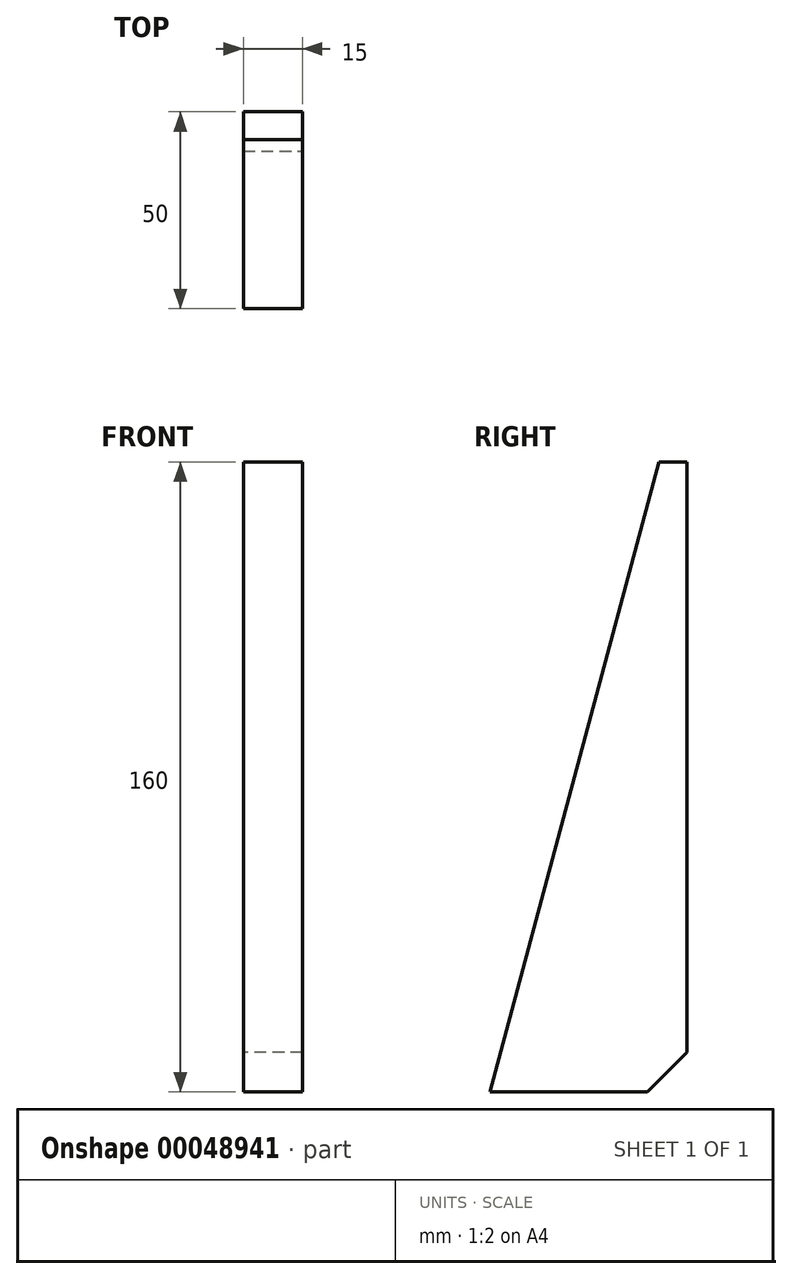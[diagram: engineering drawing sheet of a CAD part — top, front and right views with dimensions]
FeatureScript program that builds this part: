
annotation { "Feature Type Name" : "Feature", "Feature Type Description" : "" }
export const myFeature = defineFeature(function(context is Context, id is Id, definition is map)
    precondition{}
    {
        {
            var Q0;
            Q0=qCreatedBy(makeId("Right.planeOp"),FACE);
            var sketch = newSketch(context, id + "F0", { "sketchPlane" : qUnion([Q0])});
            skLineSegment(sketch, "E0", {"start": v(-92.1, -22.6) * mm, "end": v(-42.1, -22.6) * mm});
            skLineSegment(sketch, "E1", {"start": v(-42.1, -22.6) * mm, "end": v(-42.1, 137.4) * mm});
            skLineSegment(sketch, "E2", {"start": v(-92.1, -22.6) * mm, "end": v(-49.23, 137.4) * mm});
            skLineSegment(sketch, "E3", {"start": v(-49.23, 137.4) * mm, "end": v(-42.1, 137.4) * mm});
            skSolve(sketch);
        }
        {
            var Q0;
            Q0=makeQuery(id+"F0.imprint","IMPRINT",FACE,{"disambiguationData":[TD([[makeQuery(id+"F0.imprint","IMPRINT",EDGE,{"derivedFrom":sQuery(id+"F0.wireOp",EDGE,"E0")}),1.0]])]});
            extrude(context, id + "F1", {"entities" : qUnion([Q0]), "oppositeDirection" : true, "depth" : 15 * mm});
        }
        {
            var Q0;
            Q0=makeQuery(id+"F1.opExtrude","SWEPT_EDGE",EDGE,{"disambiguationData":[OSD([sQuery(id+"F0.wireOp",EDGE,"E0"),sQuery(id+"F0.wireOp",EDGE,"E1")])]});
            chamfer(context, id + "F2", {"entities" : qUnion([Q0]), "chamferType" : ChamferType.OFFSET_ANGLE, "width" : 10 * mm, "oppositeDirection" : false, "angle" : 45 * degree, "tangentPropagation" : true});
        }
    });
